# Revit family: MAVO 3
name_source: partatom
category: Equipement de génie climatique
revit_build: Autodesk Revit 2018 (Build: 20170223_1515(x64)
units: mm (PartAtom-declared; Revit-internal decimal feet)

## family parameters
Basée sur le plan de construction = Non
Classification = Aucun
Cote de connecteur circulaire = Utiliser le diamètre
Couper avec des vides une fois chargée = Non
Partagée = Non
Point de calcul de pièce = Non
Toujours verticalement = Oui
Type d'élément = Normal

## types (2) — shared parameters
BRANCHEMENT_TERRE = Oui
COS_PHI = 0.9
DEBIT_ASPI_VIDE = 40.0 m³/h
DESCR_ALIM_X = Alimentation électrique, 3G2.5mm²
DESCR_ASPI = ASPIRATION VIDE ; 40m3/h ; G1"FEM
DIAM_ASPI_VIDE = 25 mm  [stored 0.082021 ft]
DIAM_REFOUL_AIR = 15 mm  [stored 0.0492126 ft]
DIAM_REFOUL_OXY = 15 mm  [stored 0.0492126 ft]
Debit_refoulement_air = 4.5 m³/h
HAUTEUR = 1800 mm  [stored 5.90551 ft]
HAUTEUR_ARMOIRE = 1800 mm  [stored 5.90551 ft]
LARG_PORTE_DROITE = 625 mm
LONGUEUR = 430 mm
LONG_ARMOIRE = 430 mm
NEUTRE = Oui
NIVEAU_SONORE(dB(A)) = 70
OFFSET_HAUT_PM2 = 1377 mm  [stored 4.51772 ft]
OFFSET_HAUT_POIGNEE = 1061 mm  [stored 3.48097 ft]
OFFSET_LARG_PM2 = 309 mm  [stored 1.01378 ft]
OFFSET_LARG_POIGNEE = 21 mm  [stored 0.0688976 ft]
OFFSET_LONG_VANNE1 = 37 mm  [stored 0.121391 ft]
OFFSET_LONG_VANNE3 = 25 mm  [stored 0.082021 ft]
PUISS_APPARENTE = 1333 VA
PUISS_ELECT = 1 kW
TENSION_ALIM = 230 V
VANNE1 = Vanne BS FF : DN15 - G1/2" - FF (231 0002)
VANNE3 = Vanne BS FF : DN25 - G1" - FF (231 0001)
debit_refoulement_oxygene = 4.5 m³/h
ØPE = 16 mm  [stored 0.0524934 ft]

## per-type parameters (varying)
| type | DESCR_REFOUL_AIR | DESCR_REFOUL_OXYGENE | DOUBLE_ALIMENTATION | Fabricant | LARGEUR | Lien espace client | Modèle | NBR_POLES | OFFSET_LARG_PE | OFFSET_LARG_VANNE1 | OFFSET_LARG_VANNE2 | OFFSET_LARG_VANNE3 | OFFSET_LONG_PE | POIDS(Kg) | VOLUME_AIR | VOLUME_OXYGENE |
| MAVO 3 | REFOULEMENT AIR ; 4.5m3/h ; 20 m3 ; G1/2"FEM | REFOULEMENT OXYGENE ; 4.5m3/h ; 20 m3 ; G1/2"FEM | Oui |  | 1250 mm  [stored 4.10105 ft] |  |  | 3 | 1020 mm  [stored 3.34646 ft] | 190 mm | 670 mm  [stored 2.19816 ft] | 1181 mm  [stored 3.87467 ft] | 55 mm  [stored 0.180446 ft] | 195 mm  [stored 0.639764 ft] | 20.0 m³ | 20.0 m³ |
| MINI MAVO 3 | REFOULEMENT AIR ; 4.5m3/h ; 14 m3 ; G1/2"FEM | REFOULEMENT OXYGENE ; 4.5m3/h ; 14 m3 ; G1/2"FEM | Non | MILS | 1000 mm  [stored 3.28084 ft] | https://www.mils.fr | MAVO | 1 | 867 mm  [stored 2.84449 ft] | 100 mm  [stored 0.328084 ft] | 340 mm  [stored 1.11549 ft] | 931 mm  [stored 3.05446 ft] | 20 mm  [stored 0.0656168 ft] | 185 mm  [stored 0.606955 ft] | 14.0 m³ | 14.0 m³ |

note: [stored X ft] marks values corroborated as IEEE doubles in the binary element streams (Revit-internal decimal feet)

## geometry (parser evidence)
native form markers: Sweep x3
no freeform markers — native parametric forms only
